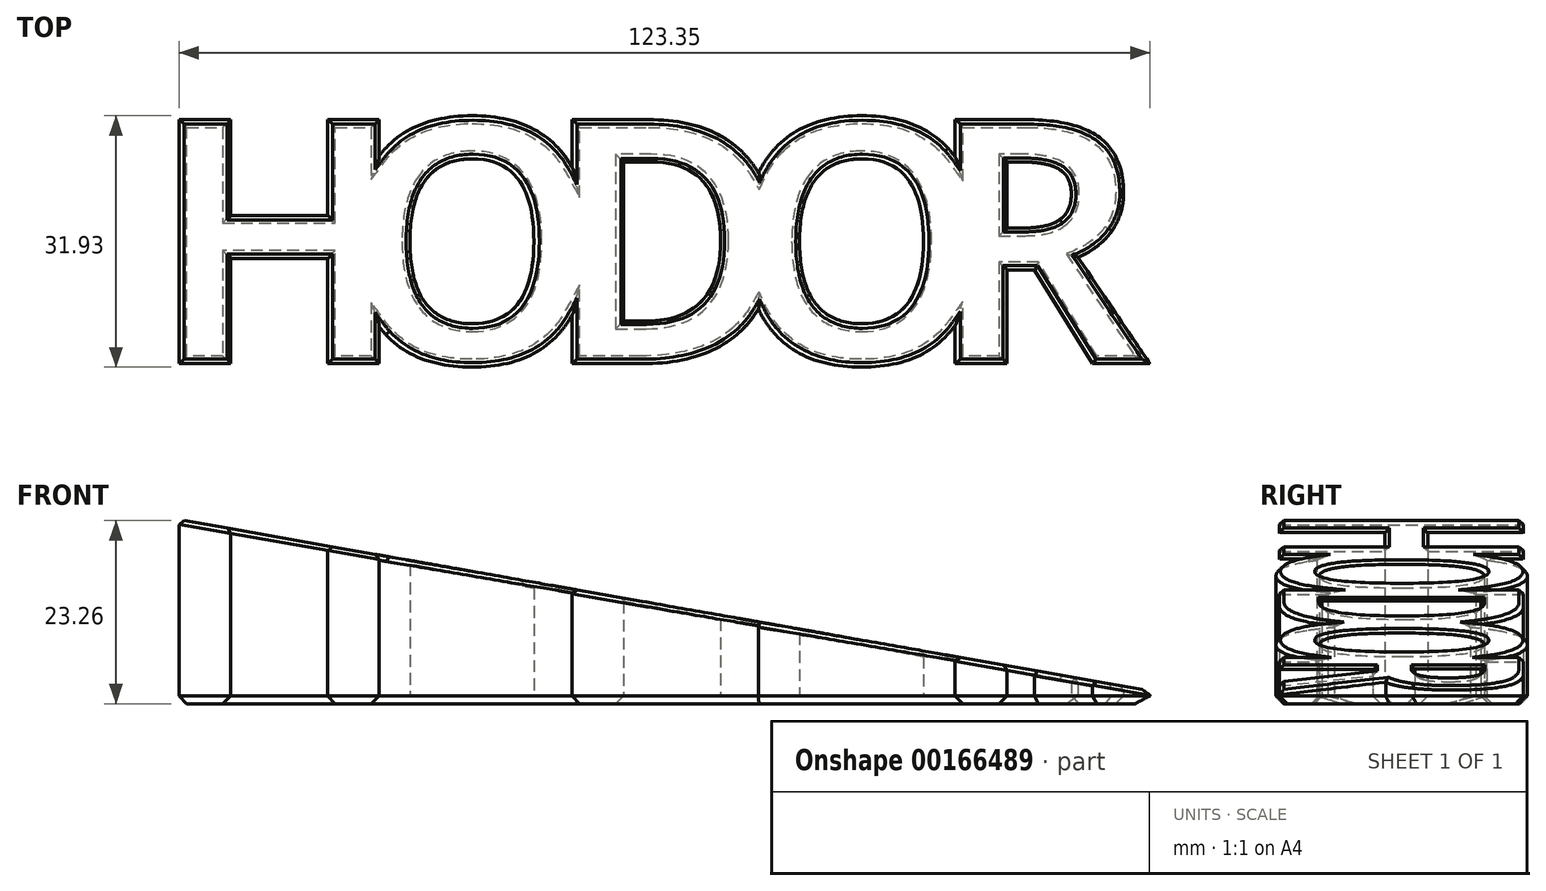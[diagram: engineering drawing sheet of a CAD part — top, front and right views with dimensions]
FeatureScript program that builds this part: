
annotation { "Feature Type Name" : "Feature", "Feature Type Description" : "" }
export const myFeature = defineFeature(function(context is Context, id is Id, definition is map)
    precondition{}
    {
        {
            var Q0;
            Q0=qCreatedBy(makeId("Top.planeOp"),FACE);
            var sketch = newSketch(context, id + "F0", { "sketchPlane" : qUnion([Q0])});
            skText(sketch, "E0", { "text": "O", "fontName": "OpenSans-Bold.ttf"});
            skText(sketch, "E1", { "text": "D", "fontName": "OpenSans-Bold.ttf"});
            skText(sketch, "E2", { "text": "H", "fontName": "OpenSans-Bold.ttf"});
            skText(sketch, "E3", { "text": "R", "fontName": "OpenSans-Bold.ttf"});
            skText(sketch, "E4", { "text": "O", "fontName": "OpenSans-Bold.ttf"});
            const initialGuessF0  = {"E0": [-0.07682, 0, 1, 0, 0.03128], "E1": [-0.05074, 0, 1, 0, 0.03128], "E2": [-0.10065, 0, 1, 0, 0.03128], "E3": [-0.00208, 0, 1, 0, 0.03128], "E4": [-0.02733, 0, 1, 0, 0.03128]};
            skSetInitialGuess(sketch, initialGuessF0);
            skSolve(sketch);
        }
        {
            var Q0;
            Q0=qCreatedBy(makeId("Right.planeOp"),FACE);
            var sketch = newSketch(context, id + "F1", { "sketchPlane" : qUnion([Q0])});
            skLineSegment(sketch, "E5", {"start": v(42.69, 6.32) * mm, "end": v(-42.3, 6.32) * mm});
            skSolve(sketch);
        }
        {
            var Q0;
            Q0=sQuery(id+"F1.wireOp",EDGE,"E5");
            var Q1;
            Q1=qCreatedBy(makeId("Top.planeOp"),FACE);
            cPlane(context, id + "F2", {"entities" : qUnion([Q0, Q1]), "cplaneType" : CPlaneType.LINE_ANGLE, "offset" : 25 * mm, "angle" : 170 * degree, "width" : 150 * mm, "height" : 150 * mm});
        }
        {
            var Q0;
            Q0 = qSketchRegion(id + "F0", true);
            var Q1;
            Q1=qCreatedBy(id+"F2.planeOp",FACE);
            extrude(context, id + "F3", {"entities" : qUnion([Q0]), "endBound" : BoundingType.UP_TO_SURFACE, "endBoundEntityFace" : qUnion([Q1]), "depth" : 25 * mm});
        }
        {
            var Q0;
            Q0=makeQuery(id+"F3.opExtrude","CAP_FACE",FACE,{"disambiguationData":[OSD([sQuery(id+"F0.wireOp",EDGE,"E0.sketch_text.stroke-0"),sQuery(id+"F0.wireOp",EDGE,"E0.sketch_text.stroke-1"),sQuery(id+"F0.wireOp",EDGE,"E0.sketch_text.stroke-2"),sQuery(id+"F0.wireOp",EDGE,"E0.sketch_text.stroke-3"),sQuery(id+"F0.wireOp",EDGE,"E0.sketch_text.stroke-4"),sQuery(id+"F0.wireOp",EDGE,"E0.sketch_text.stroke-5"),sQuery(id+"F0.wireOp",EDGE,"E0.sketch_text.stroke-6"),sQuery(id+"F0.wireOp",EDGE,"E0.sketch_text.stroke-7"),sQuery(id+"F0.wireOp",EDGE,"E0.sketch_text.stroke-8"),sQuery(id+"F0.wireOp",EDGE,"E0.sketch_text.stroke-9"),sQuery(id+"F0.wireOp",EDGE,"E0.sketch_text.stroke-10"),sQuery(id+"F0.wireOp",EDGE,"E0.sketch_text.stroke-11"),sQuery(id+"F0.wireOp",EDGE,"E0.sketch_text.stroke-12"),sQuery(id+"F0.wireOp",EDGE,"E0.sketch_text.stroke-13"),sQuery(id+"F0.wireOp",EDGE,"E1.sketch_text.stroke-0"),sQuery(id+"F0.wireOp",EDGE,"E1.sketch_text.stroke-1"),sQuery(id+"F0.wireOp",EDGE,"E1.sketch_text.stroke-2"),sQuery(id+"F0.wireOp",EDGE,"E1.sketch_text.stroke-3"),sQuery(id+"F0.wireOp",EDGE,"E1.sketch_text.stroke-4"),sQuery(id+"F0.wireOp",EDGE,"E1.sketch_text.stroke-5"),sQuery(id+"F0.wireOp",EDGE,"E1.sketch_text.stroke-6"),sQuery(id+"F0.wireOp",EDGE,"E1.sketch_text.stroke-7"),sQuery(id+"F0.wireOp",EDGE,"E1.sketch_text.stroke-8"),sQuery(id+"F0.wireOp",EDGE,"E1.sketch_text.stroke-9"),sQuery(id+"F0.wireOp",EDGE,"E1.sketch_text.stroke-10"),sQuery(id+"F0.wireOp",EDGE,"E1.sketch_text.stroke-11"),sQuery(id+"F0.wireOp",EDGE,"E2.sketch_text.stroke-0"),sQuery(id+"F0.wireOp",EDGE,"E2.sketch_text.stroke-1"),sQuery(id+"F0.wireOp",EDGE,"E2.sketch_text.stroke-2"),sQuery(id+"F0.wireOp",EDGE,"E2.sketch_text.stroke-3"),sQuery(id+"F0.wireOp",EDGE,"E2.sketch_text.stroke-4"),sQuery(id+"F0.wireOp",EDGE,"E2.sketch_text.stroke-5"),sQuery(id+"F0.wireOp",EDGE,"E2.sketch_text.stroke-6"),sQuery(id+"F0.wireOp",EDGE,"E2.sketch_text.stroke-7"),sQuery(id+"F0.wireOp",EDGE,"E2.sketch_text.stroke-8"),sQuery(id+"F0.wireOp",EDGE,"E2.sketch_text.stroke-9"),sQuery(id+"F0.wireOp",EDGE,"E2.sketch_text.stroke-10"),sQuery(id+"F0.wireOp",EDGE,"E2.sketch_text.stroke-11"),sQuery(id+"F0.wireOp",EDGE,"E3.sketch_text.stroke-0"),sQuery(id+"F0.wireOp",EDGE,"E3.sketch_text.stroke-1"),sQuery(id+"F0.wireOp",EDGE,"E3.sketch_text.stroke-2"),sQuery(id+"F0.wireOp",EDGE,"E3.sketch_text.stroke-3"),sQuery(id+"F0.wireOp",EDGE,"E3.sketch_text.stroke-4"),sQuery(id+"F0.wireOp",EDGE,"E3.sketch_text.stroke-5"),sQuery(id+"F0.wireOp",EDGE,"E3.sketch_text.stroke-6"),sQuery(id+"F0.wireOp",EDGE,"E3.sketch_text.stroke-7"),sQuery(id+"F0.wireOp",EDGE,"E3.sketch_text.stroke-8"),sQuery(id+"F0.wireOp",EDGE,"E3.sketch_text.stroke-9"),sQuery(id+"F0.wireOp",EDGE,"E3.sketch_text.stroke-10"),sQuery(id+"F0.wireOp",EDGE,"E3.sketch_text.stroke-11"),sQuery(id+"F0.wireOp",EDGE,"E3.sketch_text.stroke-12"),sQuery(id+"F0.wireOp",EDGE,"E3.sketch_text.stroke-13"),sQuery(id+"F0.wireOp",EDGE,"E3.sketch_text.stroke-14"),sQuery(id+"F0.wireOp",EDGE,"E3.sketch_text.stroke-15"),sQuery(id+"F0.wireOp",EDGE,"E3.sketch_text.stroke-16"),sQuery(id+"F0.wireOp",EDGE,"E3.sketch_text.stroke-17"),sQuery(id+"F0.wireOp",EDGE,"E3.sketch_text.stroke-18"),sQuery(id+"F0.wireOp",EDGE,"E4.sketch_text.stroke-0"),sQuery(id+"F0.wireOp",EDGE,"E4.sketch_text.stroke-1"),sQuery(id+"F0.wireOp",EDGE,"E4.sketch_text.stroke-2"),sQuery(id+"F0.wireOp",EDGE,"E4.sketch_text.stroke-3"),sQuery(id+"F0.wireOp",EDGE,"E4.sketch_text.stroke-4"),sQuery(id+"F0.wireOp",EDGE,"E4.sketch_text.stroke-5"),sQuery(id+"F0.wireOp",EDGE,"E4.sketch_text.stroke-6"),sQuery(id+"F0.wireOp",EDGE,"E4.sketch_text.stroke-7"),sQuery(id+"F0.wireOp",EDGE,"E4.sketch_text.stroke-8"),sQuery(id+"F0.wireOp",EDGE,"E4.sketch_text.stroke-9"),sQuery(id+"F0.wireOp",EDGE,"E4.sketch_text.stroke-10"),sQuery(id+"F0.wireOp",EDGE,"E4.sketch_text.stroke-11"),sQuery(id+"F0.wireOp",EDGE,"E4.sketch_text.stroke-12"),sQuery(id+"F0.wireOp",EDGE,"E4.sketch_text.stroke-13")])],"isStart":true});
            chamfer(context, id + "F4", {"entities" : qUnion([Q0]), "width" : 1 * mm, "tangentPropagation" : true});
        }
        {
            var Q0;
            Q0=makeQuery(id+"F3.opExtrude","CAP_FACE",FACE,{"disambiguationData":[OSD([sQuery(id+"F0.wireOp",EDGE,"E0.sketch_text.stroke-0"),sQuery(id+"F0.wireOp",EDGE,"E0.sketch_text.stroke-1"),sQuery(id+"F0.wireOp",EDGE,"E0.sketch_text.stroke-2"),sQuery(id+"F0.wireOp",EDGE,"E0.sketch_text.stroke-3"),sQuery(id+"F0.wireOp",EDGE,"E0.sketch_text.stroke-4"),sQuery(id+"F0.wireOp",EDGE,"E0.sketch_text.stroke-5"),sQuery(id+"F0.wireOp",EDGE,"E0.sketch_text.stroke-6"),sQuery(id+"F0.wireOp",EDGE,"E0.sketch_text.stroke-7"),sQuery(id+"F0.wireOp",EDGE,"E0.sketch_text.stroke-8"),sQuery(id+"F0.wireOp",EDGE,"E0.sketch_text.stroke-9"),sQuery(id+"F0.wireOp",EDGE,"E0.sketch_text.stroke-10"),sQuery(id+"F0.wireOp",EDGE,"E0.sketch_text.stroke-11"),sQuery(id+"F0.wireOp",EDGE,"E0.sketch_text.stroke-12"),sQuery(id+"F0.wireOp",EDGE,"E0.sketch_text.stroke-13"),sQuery(id+"F0.wireOp",EDGE,"E1.sketch_text.stroke-0"),sQuery(id+"F0.wireOp",EDGE,"E1.sketch_text.stroke-1"),sQuery(id+"F0.wireOp",EDGE,"E1.sketch_text.stroke-2"),sQuery(id+"F0.wireOp",EDGE,"E1.sketch_text.stroke-3"),sQuery(id+"F0.wireOp",EDGE,"E1.sketch_text.stroke-4"),sQuery(id+"F0.wireOp",EDGE,"E1.sketch_text.stroke-5"),sQuery(id+"F0.wireOp",EDGE,"E1.sketch_text.stroke-6"),sQuery(id+"F0.wireOp",EDGE,"E1.sketch_text.stroke-7"),sQuery(id+"F0.wireOp",EDGE,"E1.sketch_text.stroke-8"),sQuery(id+"F0.wireOp",EDGE,"E1.sketch_text.stroke-9"),sQuery(id+"F0.wireOp",EDGE,"E1.sketch_text.stroke-10"),sQuery(id+"F0.wireOp",EDGE,"E1.sketch_text.stroke-11"),sQuery(id+"F0.wireOp",EDGE,"E2.sketch_text.stroke-0"),sQuery(id+"F0.wireOp",EDGE,"E2.sketch_text.stroke-1"),sQuery(id+"F0.wireOp",EDGE,"E2.sketch_text.stroke-2"),sQuery(id+"F0.wireOp",EDGE,"E2.sketch_text.stroke-3"),sQuery(id+"F0.wireOp",EDGE,"E2.sketch_text.stroke-4"),sQuery(id+"F0.wireOp",EDGE,"E2.sketch_text.stroke-5"),sQuery(id+"F0.wireOp",EDGE,"E2.sketch_text.stroke-6"),sQuery(id+"F0.wireOp",EDGE,"E2.sketch_text.stroke-7"),sQuery(id+"F0.wireOp",EDGE,"E2.sketch_text.stroke-8"),sQuery(id+"F0.wireOp",EDGE,"E2.sketch_text.stroke-9"),sQuery(id+"F0.wireOp",EDGE,"E2.sketch_text.stroke-10"),sQuery(id+"F0.wireOp",EDGE,"E2.sketch_text.stroke-11"),sQuery(id+"F0.wireOp",EDGE,"E3.sketch_text.stroke-0"),sQuery(id+"F0.wireOp",EDGE,"E3.sketch_text.stroke-1"),sQuery(id+"F0.wireOp",EDGE,"E3.sketch_text.stroke-2"),sQuery(id+"F0.wireOp",EDGE,"E3.sketch_text.stroke-3"),sQuery(id+"F0.wireOp",EDGE,"E3.sketch_text.stroke-4"),sQuery(id+"F0.wireOp",EDGE,"E3.sketch_text.stroke-5"),sQuery(id+"F0.wireOp",EDGE,"E3.sketch_text.stroke-6"),sQuery(id+"F0.wireOp",EDGE,"E3.sketch_text.stroke-7"),sQuery(id+"F0.wireOp",EDGE,"E3.sketch_text.stroke-8"),sQuery(id+"F0.wireOp",EDGE,"E3.sketch_text.stroke-9"),sQuery(id+"F0.wireOp",EDGE,"E3.sketch_text.stroke-10"),sQuery(id+"F0.wireOp",EDGE,"E3.sketch_text.stroke-11"),sQuery(id+"F0.wireOp",EDGE,"E3.sketch_text.stroke-12"),sQuery(id+"F0.wireOp",EDGE,"E3.sketch_text.stroke-13"),sQuery(id+"F0.wireOp",EDGE,"E3.sketch_text.stroke-14"),sQuery(id+"F0.wireOp",EDGE,"E3.sketch_text.stroke-15"),sQuery(id+"F0.wireOp",EDGE,"E3.sketch_text.stroke-16"),sQuery(id+"F0.wireOp",EDGE,"E3.sketch_text.stroke-17"),sQuery(id+"F0.wireOp",EDGE,"E3.sketch_text.stroke-18"),sQuery(id+"F0.wireOp",EDGE,"E4.sketch_text.stroke-0"),sQuery(id+"F0.wireOp",EDGE,"E4.sketch_text.stroke-1"),sQuery(id+"F0.wireOp",EDGE,"E4.sketch_text.stroke-2"),sQuery(id+"F0.wireOp",EDGE,"E4.sketch_text.stroke-3"),sQuery(id+"F0.wireOp",EDGE,"E4.sketch_text.stroke-4"),sQuery(id+"F0.wireOp",EDGE,"E4.sketch_text.stroke-5"),sQuery(id+"F0.wireOp",EDGE,"E4.sketch_text.stroke-6"),sQuery(id+"F0.wireOp",EDGE,"E4.sketch_text.stroke-7"),sQuery(id+"F0.wireOp",EDGE,"E4.sketch_text.stroke-8"),sQuery(id+"F0.wireOp",EDGE,"E4.sketch_text.stroke-9"),sQuery(id+"F0.wireOp",EDGE,"E4.sketch_text.stroke-10"),sQuery(id+"F0.wireOp",EDGE,"E4.sketch_text.stroke-11"),sQuery(id+"F0.wireOp",EDGE,"E4.sketch_text.stroke-12"),sQuery(id+"F0.wireOp",EDGE,"E4.sketch_text.stroke-13")])],"isStart":false});
            chamfer(context, id + "F5", {"entities" : qUnion([Q0]), "width" : .5 * mm, "tangentPropagation" : true});
        }
    });
